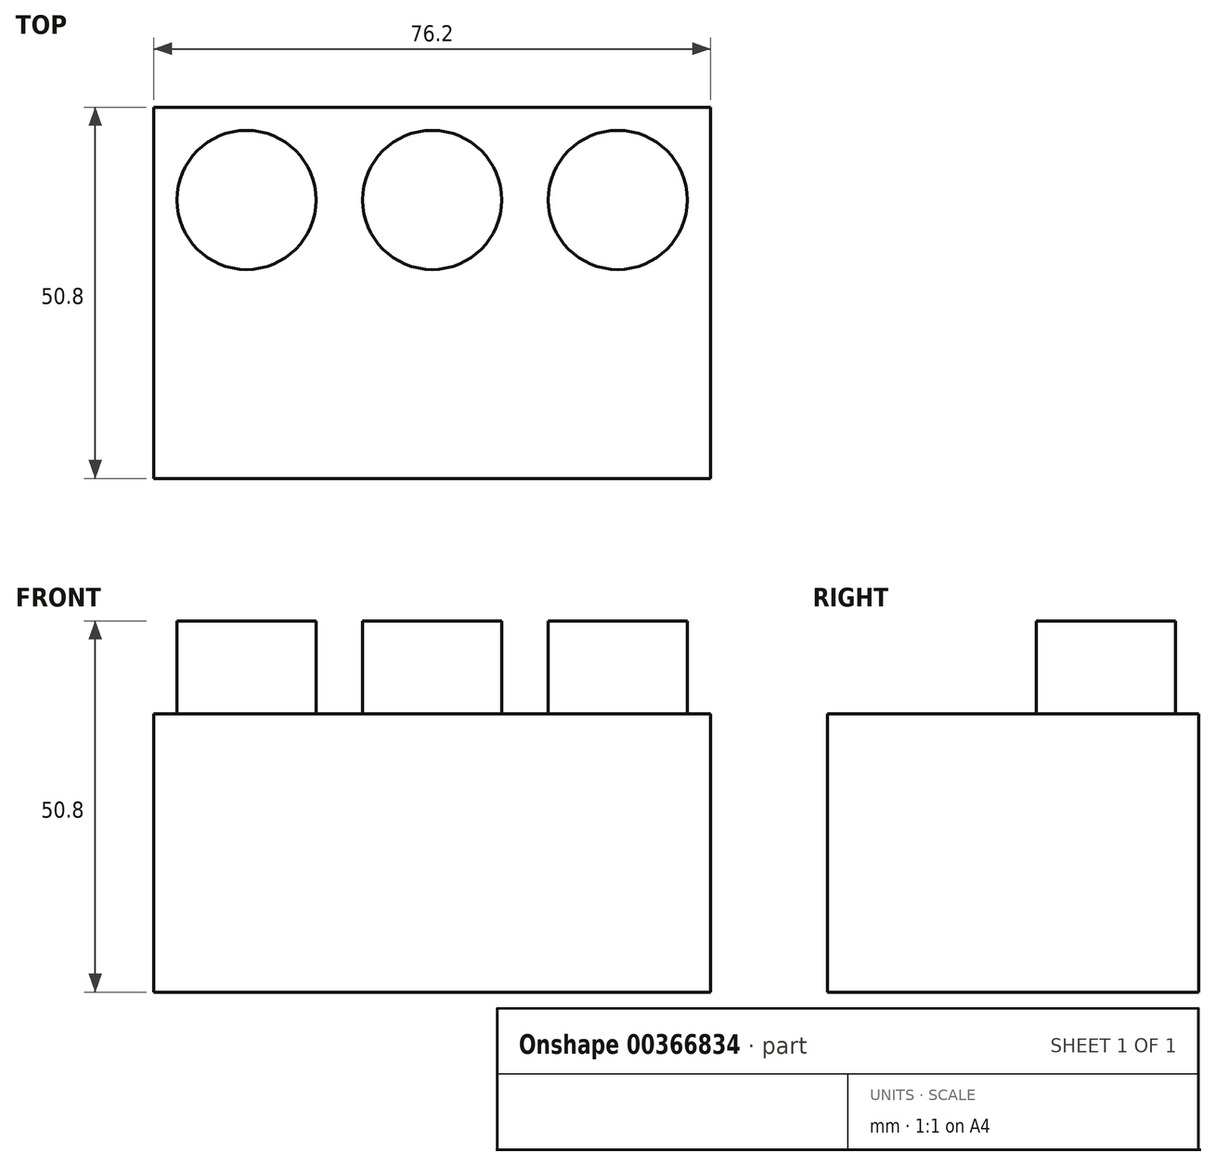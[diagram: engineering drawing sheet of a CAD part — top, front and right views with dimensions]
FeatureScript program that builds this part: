
annotation { "Feature Type Name" : "Feature", "Feature Type Description" : "" }
export const myFeature = defineFeature(function(context is Context, id is Id, definition is map)
    precondition{}
    {
        {
            var Q0;
            Q0=qCreatedBy(makeId("Top.planeOp"),FACE);
            var sketch = newSketch(context, id + "F0", { "sketchPlane" : qUnion([Q0])});
            skLineSegment(sketch, "E0.bottom", {"start": v(-38.1, 25.4) * mm, "end": v(38.1, 25.4) * mm});
            skLineSegment(sketch, "E0.top", {"start": v(-38.1, -25.4) * mm, "end": v(38.1, -25.4) * mm});
            skLineSegment(sketch, "E0.left", {"start": v(-38.1, 25.4) * mm, "end": v(-38.1, -25.4) * mm});
            skLineSegment(sketch, "E0.right", {"start": v(38.1, 25.4) * mm, "end": v(38.1, -25.4) * mm});
            skPoint(sketch, "E0.middle", {"position": v(0, 0) * mm});
            skSolve(sketch);
        }
        {
            var Q0;
            Q0=makeQuery(id+"F0.imprint","IMPRINT",FACE,{"disambiguationData":[TD([[makeQuery(id+"F0.imprint","IMPRINT",EDGE,{"derivedFrom":sQuery(id+"F0.wireOp",EDGE,"E0.bottom")}),-1.0]])]});
            extrude(context, id + "F1", {"entities" : qUnion([Q0]), "depth" : 38.1 * mm});
        }
        {
            var Q0;
            Q0=makeQuery(id+"F1.opExtrude","CAP_FACE",FACE,{"disambiguationData":[OSD([sQuery(id+"F0.wireOp",EDGE,"E0.bottom"),sQuery(id+"F0.wireOp",EDGE,"E0.top"),sQuery(id+"F0.wireOp",EDGE,"E0.left"),sQuery(id+"F0.wireOp",EDGE,"E0.right")])],"isStart":false});
            var sketch = newSketch(context, id + "F2", { "sketchPlane" : qUnion([Q0])});
            skCircle(sketch, "E1", {"center": v(-25.4, 12.7) * mm, "radius": 9.53 * mm});
            skCircle(sketch, "E2", {"center": v(0, 12.7) * mm, "radius": 9.53 * mm});
            skCircle(sketch, "E3", {"center": v(25.4, 12.7) * mm, "radius": 9.53 * mm});
            skSolve(sketch);
        }
        {
            var Q0;
            Q0=makeQuery(id+"F2.imprint","IMPRINT",FACE,{"disambiguationData":[TD([[makeQuery(id+"F2.imprint","IMPRINT",EDGE,{"derivedFrom":sQuery(id+"F2.wireOp",EDGE,"E1")}),1.0]])]});
            var Q1;
            Q1=makeQuery(id+"F2.imprint","IMPRINT",FACE,{"disambiguationData":[TD([[makeQuery(id+"F2.imprint","IMPRINT",EDGE,{"derivedFrom":sQuery(id+"F2.wireOp",EDGE,"E2")}),1.0]])]});
            var Q2;
            Q2=makeQuery(id+"F2.imprint","IMPRINT",FACE,{"disambiguationData":[TD([[makeQuery(id+"F2.imprint","IMPRINT",EDGE,{"derivedFrom":sQuery(id+"F2.wireOp",EDGE,"E3")}),1.0]])]});
            extrude(context, id + "F3", {"entities" : qUnion([Q0, Q1, Q2]), "operationType" : NewBodyOperationType.ADD, "depth" : 12.7 * mm});
        }
    });
